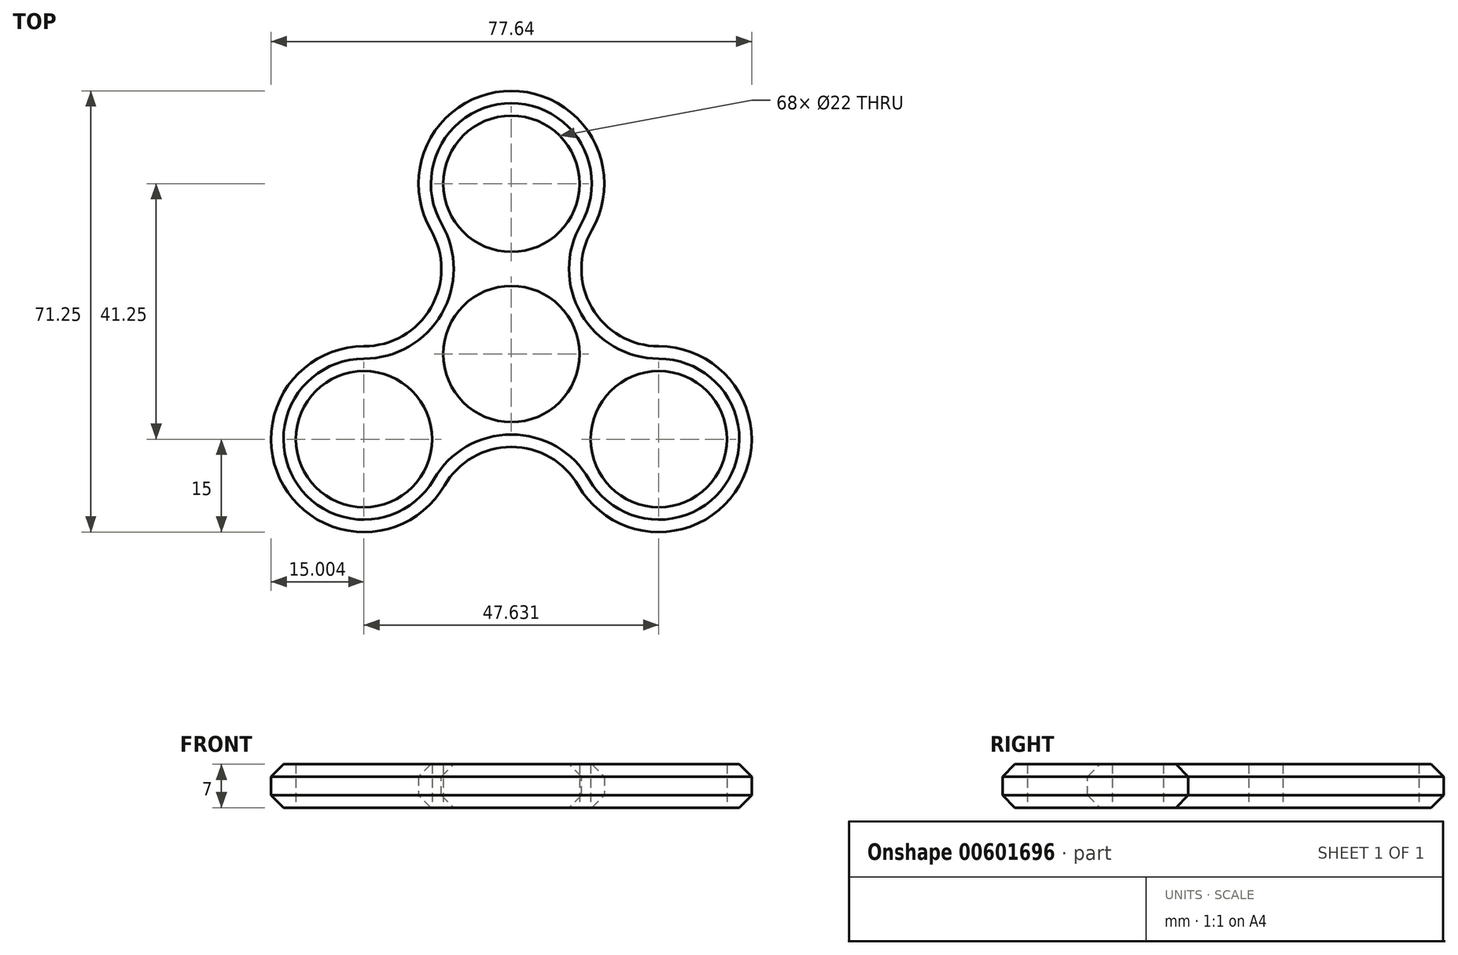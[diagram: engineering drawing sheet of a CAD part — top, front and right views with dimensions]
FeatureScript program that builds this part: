
annotation { "Feature Type Name" : "Feature", "Feature Type Description" : "" }
export const myFeature = defineFeature(function(context is Context, id is Id, definition is map)
    precondition{}
    {
        {
            var Q0;
            Q0=qCreatedBy(makeId("Top.planeOp"),FACE);
            var sketch = newSketch(context, id + "F0", { "sketchPlane" : qUnion([Q0])});
            skCircle(sketch, "E0", {"center": v(0, 0) * mm, "radius": 11 * mm});
            skLineSegment(sketch, "E1", {"start": v(0, 0) * mm, "end": v(0, 27.5) * mm, "construction": true});
            skCircle(sketch, "E2", {"center": v(0, 27.5) * mm, "radius": 11 * mm});
            skCircle(sketch, "E3.1.0", {"center": v(-23.82, -13.75) * mm, "radius": 11 * mm});
            skCircle(sketch, "E3.2.0", {"center": v(23.82, -13.75) * mm, "radius": 11 * mm});
            skCircle(sketch, "E4", {"center": v(0, 0) * mm, "radius": 15 * mm});
            skCircle(sketch, "E5", {"center": v(0, 27.5) * mm, "radius": 15 * mm});
            skCircle(sketch, "E6.1.0", {"center": v(-23.82, -13.75) * mm, "radius": 15 * mm});
            skCircle(sketch, "E6.2.0", {"center": v(23.82, -13.75) * mm, "radius": 15 * mm});
            skSolve(sketch);
        }
        {
            var Q0;
            Q0 = qSketchRegion(id + "F0", true);
            extrude(context, id + "F1", {"entities" : qUnion([Q0]), "depth" : 7 * mm, "offsetDistance" : 25 * mm});
        }
        {
            var Q0;
            {var subQ0=sQuery(id+"F0.wireOp",EDGE,"E5");var subQ1=sQuery(id+"F0.wireOp",EDGE,"E4");Q0=makeQuery(id+"F1.opExtrude","SWEPT_EDGE",EDGE,{"disambiguationData":[OSD([subQ1,subQ0]),TDD([makeQuery(id+"F0.imprint","INTERSECT",VERTEX,{"disambiguationData":[OD(1.0)],"derivedFrom":[subQ1,subQ0]})])]});}
            var Q1;
            {var subQ0=sQuery(id+"F0.wireOp",EDGE,"E6.2.0");var subQ1=sQuery(id+"F0.wireOp",EDGE,"E4");Q1=makeQuery(id+"F1.opExtrude","SWEPT_EDGE",EDGE,{"disambiguationData":[OSD([subQ1,subQ0]),TDD([makeQuery(id+"F0.imprint","INTERSECT",VERTEX,{"disambiguationData":[OD(1.0)],"derivedFrom":[subQ1,subQ0]})])]});}
            var Q2;
            {var subQ0=sQuery(id+"F0.wireOp",EDGE,"E6.1.0");var subQ1=sQuery(id+"F0.wireOp",EDGE,"E4");Q2=makeQuery(id+"F1.opExtrude","SWEPT_EDGE",EDGE,{"disambiguationData":[OSD([subQ1,subQ0]),TDD([makeQuery(id+"F0.imprint","INTERSECT",VERTEX,{"disambiguationData":[OD(0.0)],"derivedFrom":[subQ1,subQ0]})])]});}
            var Q3;
            {var subQ0=sQuery(id+"F0.wireOp",EDGE,"E5");var subQ1=sQuery(id+"F0.wireOp",EDGE,"E4");Q3=makeQuery(id+"F1.opExtrude","SWEPT_EDGE",EDGE,{"disambiguationData":[OSD([subQ1,subQ0]),TDD([makeQuery(id+"F0.imprint","INTERSECT",VERTEX,{"disambiguationData":[OD(0.0)],"derivedFrom":[subQ1,subQ0]})])]});}
            var Q4;
            {var subQ0=sQuery(id+"F0.wireOp",EDGE,"E6.1.0");var subQ1=sQuery(id+"F0.wireOp",EDGE,"E4");Q4=makeQuery(id+"F1.opExtrude","SWEPT_EDGE",EDGE,{"disambiguationData":[OSD([subQ1,subQ0]),TDD([makeQuery(id+"F0.imprint","INTERSECT",VERTEX,{"disambiguationData":[OD(1.0)],"derivedFrom":[subQ1,subQ0]})])]});}
            var Q5;
            {var subQ0=sQuery(id+"F0.wireOp",EDGE,"E6.2.0");var subQ1=sQuery(id+"F0.wireOp",EDGE,"E4");Q5=makeQuery(id+"F1.opExtrude","SWEPT_EDGE",EDGE,{"disambiguationData":[OSD([subQ1,subQ0]),TDD([makeQuery(id+"F0.imprint","INTERSECT",VERTEX,{"disambiguationData":[OD(0.0)],"derivedFrom":[subQ1,subQ0]})])]});}
            fillet(context, id + "F2", {"entities" : qUnion([Q0, Q1, Q2, Q3, Q4, Q5]), "radius" : 12.5 * mm, "tangentPropagation" : true, "allowEdgeOverflow" : false});
        }
        {
            var Q0;
            {var subQ0=sQuery(id+"F0.wireOp",EDGE,"E6.1.0");var subQ1=sQuery(id+"F0.wireOp",EDGE,"E4");Q0=makeQuery(id+"F2.opFillet","BLEND_EDGE",EDGE,{"blendedFrom":[makeQuery(id+"F1.opExtrude","SWEPT_EDGE",EDGE,{"disambiguationData":[OSD([subQ1,subQ0]),TDD([makeQuery(id+"F0.imprint","INTERSECT",VERTEX,{"disambiguationData":[OD(1.0)],"derivedFrom":[subQ1,subQ0]})])]}),makeQuery(id+"F1.opExtrude","CAP_FACE",FACE,{"disambiguationData":[OSD([sQuery(id+"F0.wireOp",EDGE,"E0"),sQuery(id+"F0.wireOp",EDGE,"E2"),sQuery(id+"F0.wireOp",EDGE,"E3.1.0"),sQuery(id+"F0.wireOp",EDGE,"E3.2.0"),subQ1,sQuery(id+"F0.wireOp",EDGE,"E5"),subQ0,sQuery(id+"F0.wireOp",EDGE,"E6.2.0")])],"isStart":true})],"blendedInto":[makeQuery(id+"F1.opExtrude","CAP_FACE",FACE,{"disambiguationData":[OSD([sQuery(id+"F0.wireOp",EDGE,"E0"),sQuery(id+"F0.wireOp",EDGE,"E2"),sQuery(id+"F0.wireOp",EDGE,"E3.1.0"),sQuery(id+"F0.wireOp",EDGE,"E3.2.0"),subQ1,sQuery(id+"F0.wireOp",EDGE,"E5"),subQ0,sQuery(id+"F0.wireOp",EDGE,"E6.2.0")])],"isStart":true})]});}
            var Q1;
            {var subQ0=sQuery(id+"F0.wireOp",EDGE,"E6.1.0");var subQ1=sQuery(id+"F0.wireOp",EDGE,"E4");Q1=makeQuery(id+"F2.opFillet","BLEND_EDGE",EDGE,{"blendedFrom":[makeQuery(id+"F1.opExtrude","SWEPT_EDGE",EDGE,{"disambiguationData":[OSD([subQ1,subQ0]),TDD([makeQuery(id+"F0.imprint","INTERSECT",VERTEX,{"disambiguationData":[OD(1.0)],"derivedFrom":[subQ1,subQ0]})])]}),makeQuery(id+"F1.opExtrude","CAP_FACE",FACE,{"disambiguationData":[OSD([sQuery(id+"F0.wireOp",EDGE,"E0"),sQuery(id+"F0.wireOp",EDGE,"E2"),sQuery(id+"F0.wireOp",EDGE,"E3.1.0"),sQuery(id+"F0.wireOp",EDGE,"E3.2.0"),subQ1,sQuery(id+"F0.wireOp",EDGE,"E5"),subQ0,sQuery(id+"F0.wireOp",EDGE,"E6.2.0")])],"isStart":false})],"blendedInto":[makeQuery(id+"F1.opExtrude","CAP_FACE",FACE,{"disambiguationData":[OSD([sQuery(id+"F0.wireOp",EDGE,"E0"),sQuery(id+"F0.wireOp",EDGE,"E2"),sQuery(id+"F0.wireOp",EDGE,"E3.1.0"),sQuery(id+"F0.wireOp",EDGE,"E3.2.0"),subQ1,sQuery(id+"F0.wireOp",EDGE,"E5"),subQ0,sQuery(id+"F0.wireOp",EDGE,"E6.2.0")])],"isStart":false})]});}
            chamfer(context, id + "F3", {"entities" : qUnion([Q0, Q1]), "width" : 2 * mm, "tangentPropagation" : true});
        }
    });
